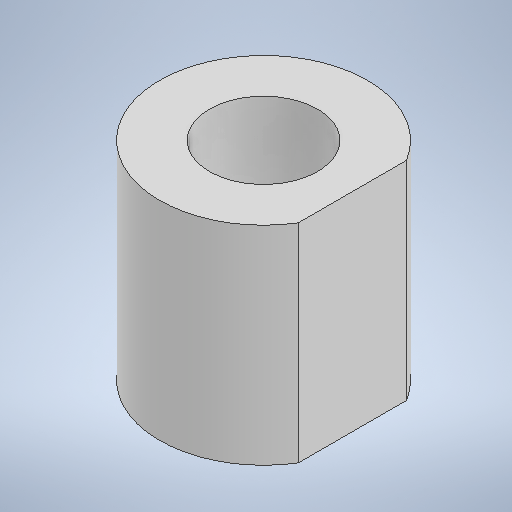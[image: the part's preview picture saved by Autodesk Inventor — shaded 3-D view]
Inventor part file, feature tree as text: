
AUTODESK INVENTOR PART (.ipt)
format: ipt  version: 2025 (Build 290162000, 162)  size: 201,216 bytes
history: native  units: mm
features: extrude x1, sketch x1
ambient origin geometry x8: Origin, YZ Plane, XZ Plane, XY Plane, X Axis, Y Axis, Z Axis, Center Point
bodies: Solid1 (feature_tree)
feature tree (2):
  extrude  "Extrusion1"  Depth=10.0mm
  sketch  "Sketch1"  dims[d0=5.2mm d1=10.0mm d2=10.0mm d3=0.0mm]
